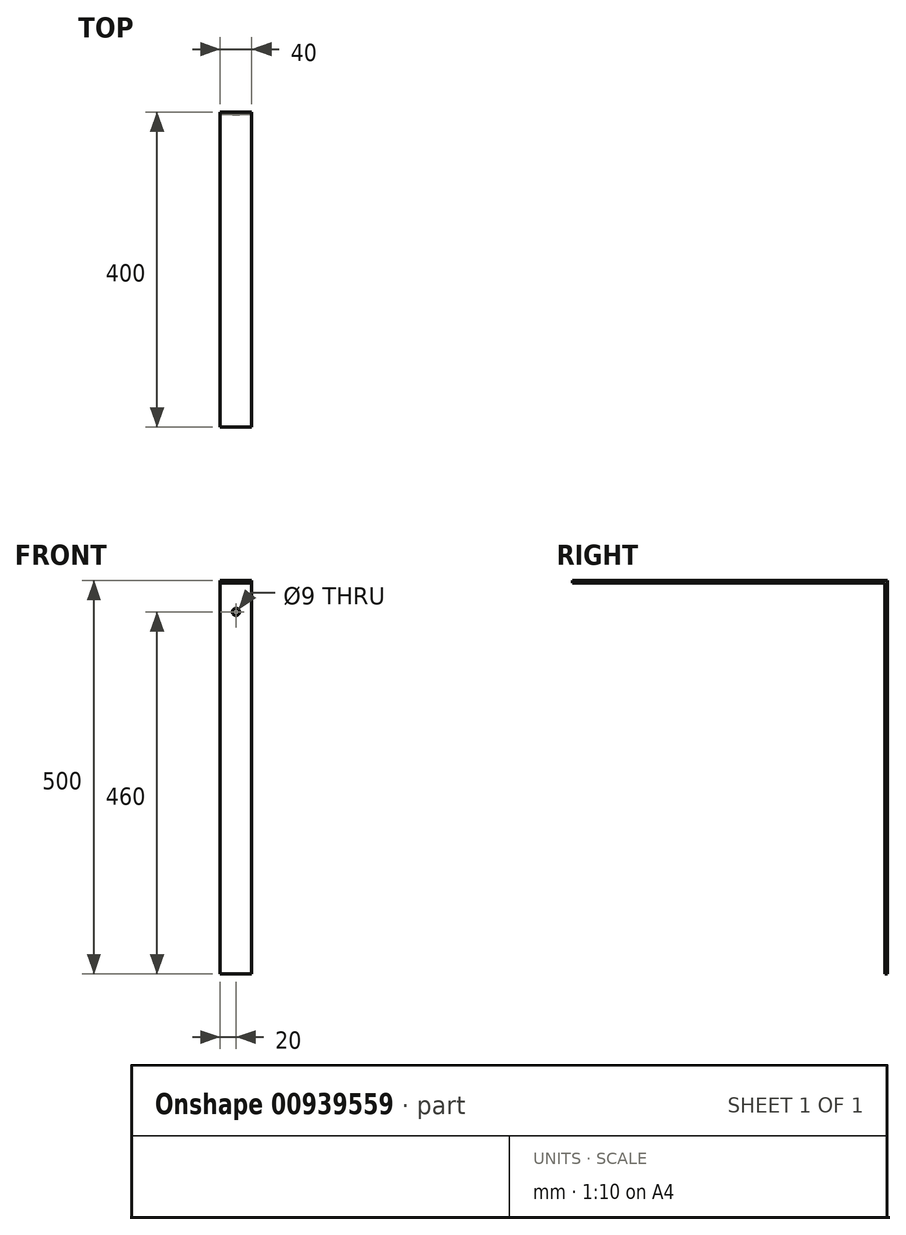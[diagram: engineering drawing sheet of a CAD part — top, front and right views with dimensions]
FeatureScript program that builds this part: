
annotation { "Feature Type Name" : "Feature", "Feature Type Description" : "" }
export const myFeature = defineFeature(function(context is Context, id is Id, definition is map)
    precondition{}
    {
        {
            var Q0;
            Q0=qCreatedBy(makeId("Right.planeOp"),FACE);
            var sketch = newSketch(context, id + "F0", { "sketchPlane" : qUnion([Q0])});
            skLineSegment(sketch, "E0", {"start": v(0, 0) * mm, "end": v(0, 500) * mm});
            skLineSegment(sketch, "E1", {"start": v(0, 500) * mm, "end": v(-400, 500) * mm});
            skLineSegment(sketch, "E2", {"start": v(-400, 500) * mm, "end": v(-400, 497) * mm});
            skLineSegment(sketch, "E3", {"start": v(-400, 497) * mm, "end": v(-3, 497) * mm});
            skLineSegment(sketch, "E4", {"start": v(-3, 497) * mm, "end": v(-3, 0) * mm});
            skLineSegment(sketch, "E5", {"start": v(-3, 0) * mm, "end": v(0, 0) * mm});
            skSolve(sketch);
        }
        {
            var Q0;
            Q0 = qSketchRegion(id + "F0", true);
            extrude(context, id + "F1", {"entities" : qUnion([Q0]), "depth" : 40 * mm, "offsetDistance" : 25 * mm});
        }
        {
            var Q0;
            Q0=makeQuery(id+"F1.opExtrude","SWEPT_FACE",FACE,{"disambiguationData":[OSD([sQuery(id+"F0.wireOp",EDGE,"E0")])]});
            var sketch = newSketch(context, id + "F2", { "sketchPlane" : qUnion([Q0])});
            skCircle(sketch, "E6", {"center": v(-20, 460) * mm, "radius": 4.5 * mm});
            skSolve(sketch);
        }
        {
            var Q0;
            Q0=makeQuery(id+"F2.imprint","IMPRINT",FACE,{"disambiguationData":[TD([[makeQuery(id+"F2.imprint","IMPRINT",EDGE,{"derivedFrom":sQuery(id+"F2.wireOp",EDGE,"E6")}),1.0]])]});
            extrude(context, id + "F3", {"entities" : qUnion([Q0]), "operationType" : NewBodyOperationType.REMOVE, "endBound" : BoundingType.THROUGH_ALL, "oppositeDirection" : true, "depth" : 25 * mm, "offsetDistance" : 25 * mm});
        }
    });
